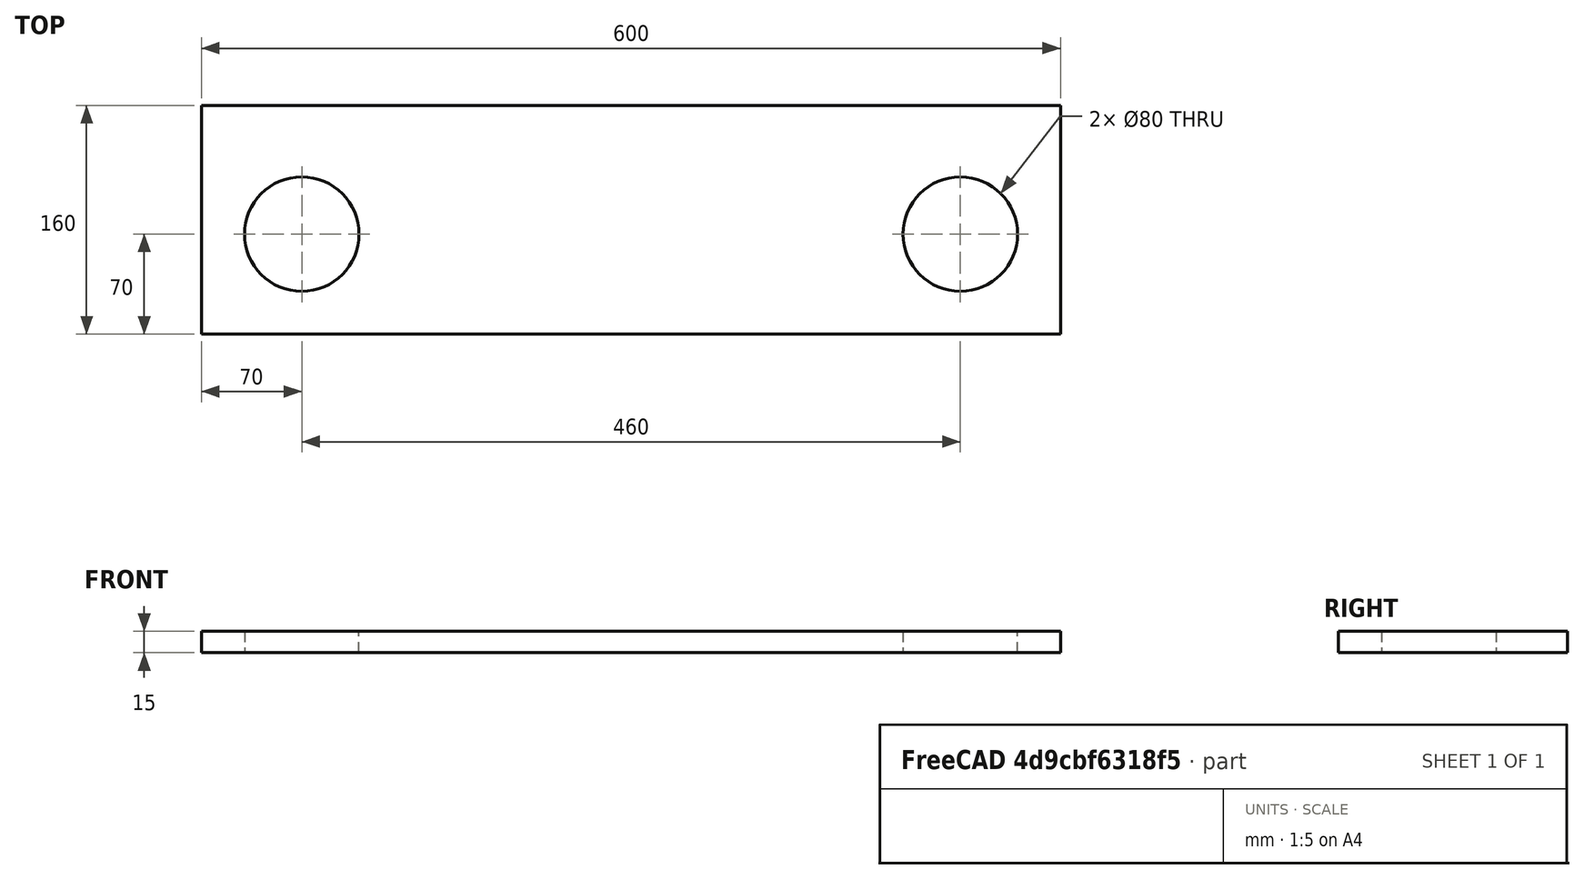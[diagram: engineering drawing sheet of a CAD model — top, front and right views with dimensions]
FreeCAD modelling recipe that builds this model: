
FCSTD DOCUMENT  (FreeCAD 1.0R39319 (Git))
Label: speaker_panel
License: All rights reserved
LicenseURL: http://en.wikipedia.org/wiki/All_rights_reserved
objects: Sketcher::SketchObject×1, PartDesign::Pad×1, PartDesign::Body×1
note: 6 computed .brp shape members not serialized (recipe doc carries the construction recipe); baked Part::Feature solids carry a one-line shape summary decoded from their .brp

FEATURE [Sketcher::SketchObject] Sketch  label="speaker_sketch"
  ArcFitTolerance = 0
  AttachmentSupport = -> [XY_Plane]
  FullyConstrained = true
  MakeInternals = false
  MapMode = 5
  sketch-geometry (10):
    g0: LineSegment StartX=0 StartY=0 StartZ=0 EndX=600 EndY=0 EndZ=0
    g1: LineSegment StartX=600 StartY=0 StartZ=0 EndX=600 EndY=160 EndZ=0
    g2: LineSegment StartX=600 StartY=160 StartZ=0 EndX=0 EndY=160 EndZ=0
    g3: LineSegment StartX=0 StartY=160 StartZ=0 EndX=0 EndY=0 EndZ=0
    g4: Circle CenterX=70 CenterY=70 CenterZ=0 NormalX=0 NormalY=0 NormalZ=1 AngleXU=0 Radius=40
    g5: Circle CenterX=530 CenterY=70 CenterZ=0 NormalX=0 NormalY=0 NormalZ=1 AngleXU=0 Radius=40
    g6: LineSegment [constr] StartX=70 StartY=70 StartZ=0 EndX=70 EndY=0 EndZ=0
    g7: LineSegment [constr] StartX=70 StartY=70 StartZ=0 EndX=0 EndY=70 EndZ=0
    g8: LineSegment [constr] StartX=530 StartY=70 StartZ=0 EndX=600 EndY=70 EndZ=0
    g9: LineSegment [constr] StartX=530 StartY=70 StartZ=0 EndX=530 EndY=0 EndZ=0
  constraints (29):
    c: Coincident(g0,g1)
    c: Coincident(g1,g2)
    c: Coincident(g2,g3)
    c: Coincident(g3,g0)
    c: Horizontal(g0)
    c: Horizontal(g2)
    c: Vertical(g1)
    c: Vertical(g3)
    c: Coincident(g0,g-1)
    c: DistanceX(g0,g0) = 600
    c: DistanceY(g3,g3) = 160
    c: Radius(g4) = 40
    c: Radius(g5) = 40
    c: Coincident(g6,g4)
    c: PointOnObject(g6,g0)
    c: Vertical(g6)
    c: PointOnObject(g7,g3)
    c: Horizontal(g7)
    c: Coincident(g8,g5)
    c: PointOnObject(g8,g1)
    c: Horizontal(g8)
    c: Coincident(g9,g5)
    c: PointOnObject(g9,g0)
    c: Vertical(g9)
    c: Equal(g7,g8)
    c: Coincident(g7,g4)
    c: Equal(g6,g9)
    c: DistanceX(g7,g7) = 70
    c: DistanceY(g6,g6) = 70
FEATURE [PartDesign::Pad] Pad  label="speaker_panel_pad"
  AllowMultiFace = false
  Direction = (0,0,1)
  Length = 15
  Length2 = 100
  Profile = -> Sketch
  ReferenceAxis = -> Sketch [N_Axis]
  Suppressed = false
  Type = 0
FEATURE [PartDesign::Body] Body  label="speaker_panel_body"
  AllowCompound = false
  Group = -> [Sketch,Pad]
  Origin = -> Origin
  Tip = -> Pad
